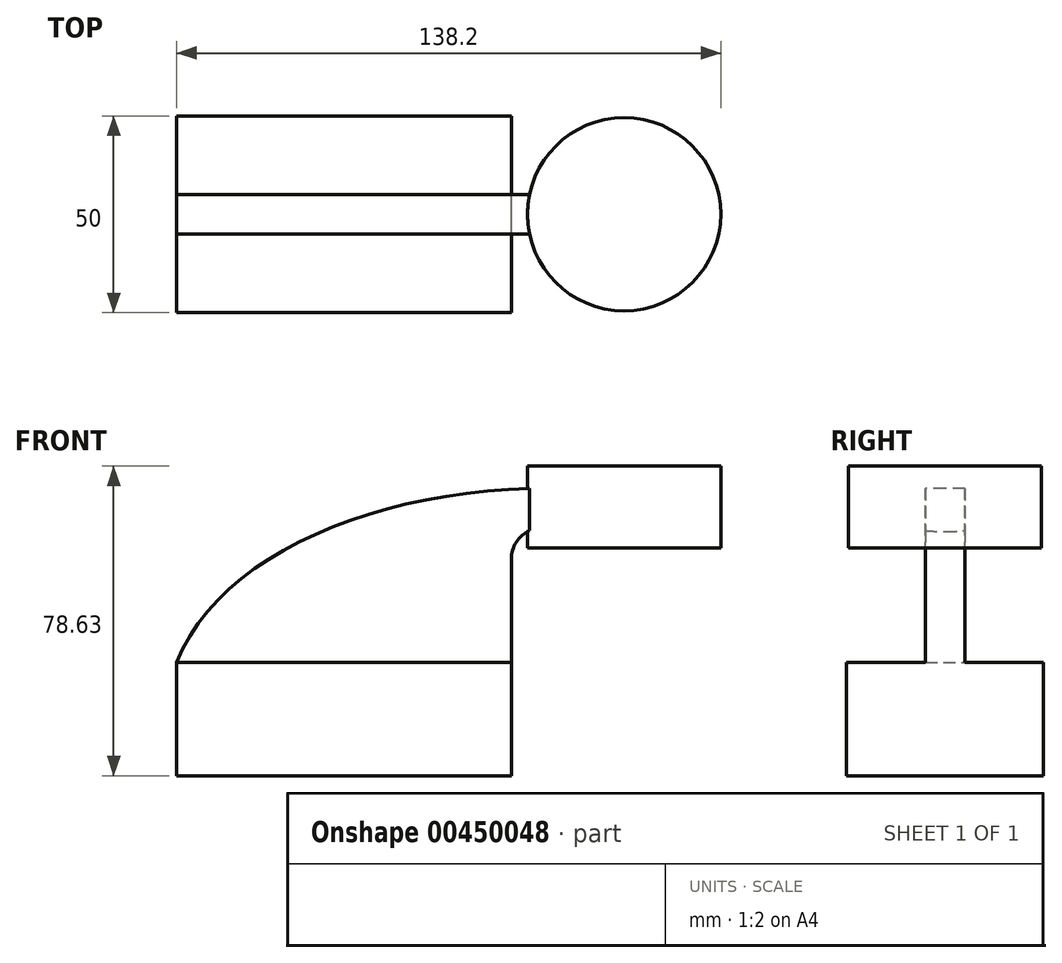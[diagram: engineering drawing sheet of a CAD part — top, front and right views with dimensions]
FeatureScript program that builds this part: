
annotation { "Feature Type Name" : "Feature", "Feature Type Description" : "" }
export const myFeature = defineFeature(function(context is Context, id is Id, definition is map)
    precondition{}
    {
        {
            var Q0;
            Q0=qCreatedBy(makeId("Front.planeOp"),FACE);
            var sketch = newSketch(context, id + "F0", { "sketchPlane" : qUnion([Q0])});
            skLineSegment(sketch, "E0.bottom", {"start": v(-42.5, 14.41) * mm, "end": v(42.5, 14.41) * mm});
            skLineSegment(sketch, "E0.top", {"start": v(-42.5, -14.41) * mm, "end": v(42.5, -14.41) * mm});
            skLineSegment(sketch, "E0.left", {"start": v(-42.5, 14.41) * mm, "end": v(-42.5, -14.41) * mm});
            skLineSegment(sketch, "E0.right", {"start": v(42.5, 14.41) * mm, "end": v(42.5, -14.41) * mm});
            skPoint(sketch, "E0.middle", {"position": v(0, 0) * mm});
            skLineSegment(sketch, "E1.bottom", {"start": v(65.72, 43.47) * mm, "end": v(95.7, 43.47) * mm});
            skLineSegment(sketch, "E1.top", {"start": v(65.72, 64.22) * mm, "end": v(95.7, 64.22) * mm});
            skLineSegment(sketch, "E1.left", {"start": v(65.72, 43.47) * mm, "end": v(65.72, 64.22) * mm});
            skLineSegment(sketch, "E1.right", {"start": v(95.7, 43.47) * mm, "end": v(95.7, 64.22) * mm});
            skPoint(sketch, "E1.middle", {"position": v(80.71, 53.85) * mm});
            skLineSegment(sketch, "E2", {"start": v(42.5, 14.41) * mm, "end": v(42.5, 40.59) * mm});
            skArc(sketch, "E3", {"start": v(42.5, 40.59) * mm, "mid": v(44.84, 46.24) * mm, "end": v(50.5, 48.59) * mm});
            skLineSegment(sketch, "E4", {"start": v(50.5, 48.59) * mm, "end": v(71.17, 48.59) * mm});
            skLineSegment(sketch, "E5.0", {"start": v(50.5, 58.59) * mm, "end": v(71.17, 58.59) * mm});
            skArc(sketch, "E5.1", {"start": v(32.5, 40.59) * mm, "mid": v(37.77, 53.32) * mm, "end": v(50.5, 58.59) * mm});
            skLineSegment(sketch, "E5.2", {"start": v(32.5, 14.41) * mm, "end": v(32.5, 40.59) * mm});
            skFitSpline(sketch, "E6", {"points": [v(-42.5, 14.41) * mm, v(50.5, 58.59) * mm], "startDerivative": vector(32.51, 81.63) * mm, "endDerivative": vector(128.94, 1.2) * mm});
            skLineSegment(sketch, "E7", {"start": v(71.17, 43.47) * mm, "end": v(71.17, 64.22) * mm});
            skSolve(sketch);
        }
        {
            var Q0;
            Q0=makeQuery(id+"F0.imprint","IMPRINT",FACE,{"disambiguationData":[TD([[makeQuery(id+"F0.imprint","IMPRINT",EDGE,{"derivedFrom":sQuery(id+"F0.wireOp",EDGE,"E0.top")}),1.0]])]});
            extrude(context, id + "F1", {"entities" : qUnion([Q0]), "endBound" : BoundingType.SYMMETRIC, "depth" : 50 * mm});
        }
        {
            var Q0;
            {var subQ1=sQuery(id+"F0.wireOp",EDGE,"E2");Q0=makeQuery(id+"F0.imprint","IMPRINT",FACE,{"disambiguationData":[TD([[makeQuery(id+"F0.imprint","IMPRINT",EDGE,{"derivedFrom":subQ1}),1.0]])]});}
            var Q1;
            {var subQ3=sQuery(id+"F0.wireOp",EDGE,"E5.2");Q1=makeQuery(id+"F0.imprint","IMPRINT",FACE,{"disambiguationData":[TD([[makeQuery(id+"F0.imprint","IMPRINT",EDGE,{"derivedFrom":subQ3}),1.0]])]});}
            extrude(context, id + "F2", {"entities" : qUnion([Q0, Q1]), "operationType" : NewBodyOperationType.ADD, "endBound" : BoundingType.SYMMETRIC, "depth" : 10 * mm});
        }
        {
            var Q0;
            {var subQ4=sQuery(id+"F0.wireOp",EDGE,"E1.right");Q0=makeQuery(id+"F0.imprint","IMPRINT",FACE,{"disambiguationData":[TD([[makeQuery(id+"F0.imprint","IMPRINT",EDGE,{"derivedFrom":subQ4}),1.0]])]});}
            var Q1;
            Q1=sQuery(id+"F0.wireOp",EDGE,"E7");
            revolve(context, id + "F3", {"operationType" : NewBodyOperationType.ADD, "entities" : qUnion([Q0]), "axis" : qUnion([Q1]), "revolveType" : RevolveType.FULL});
        }
    });
